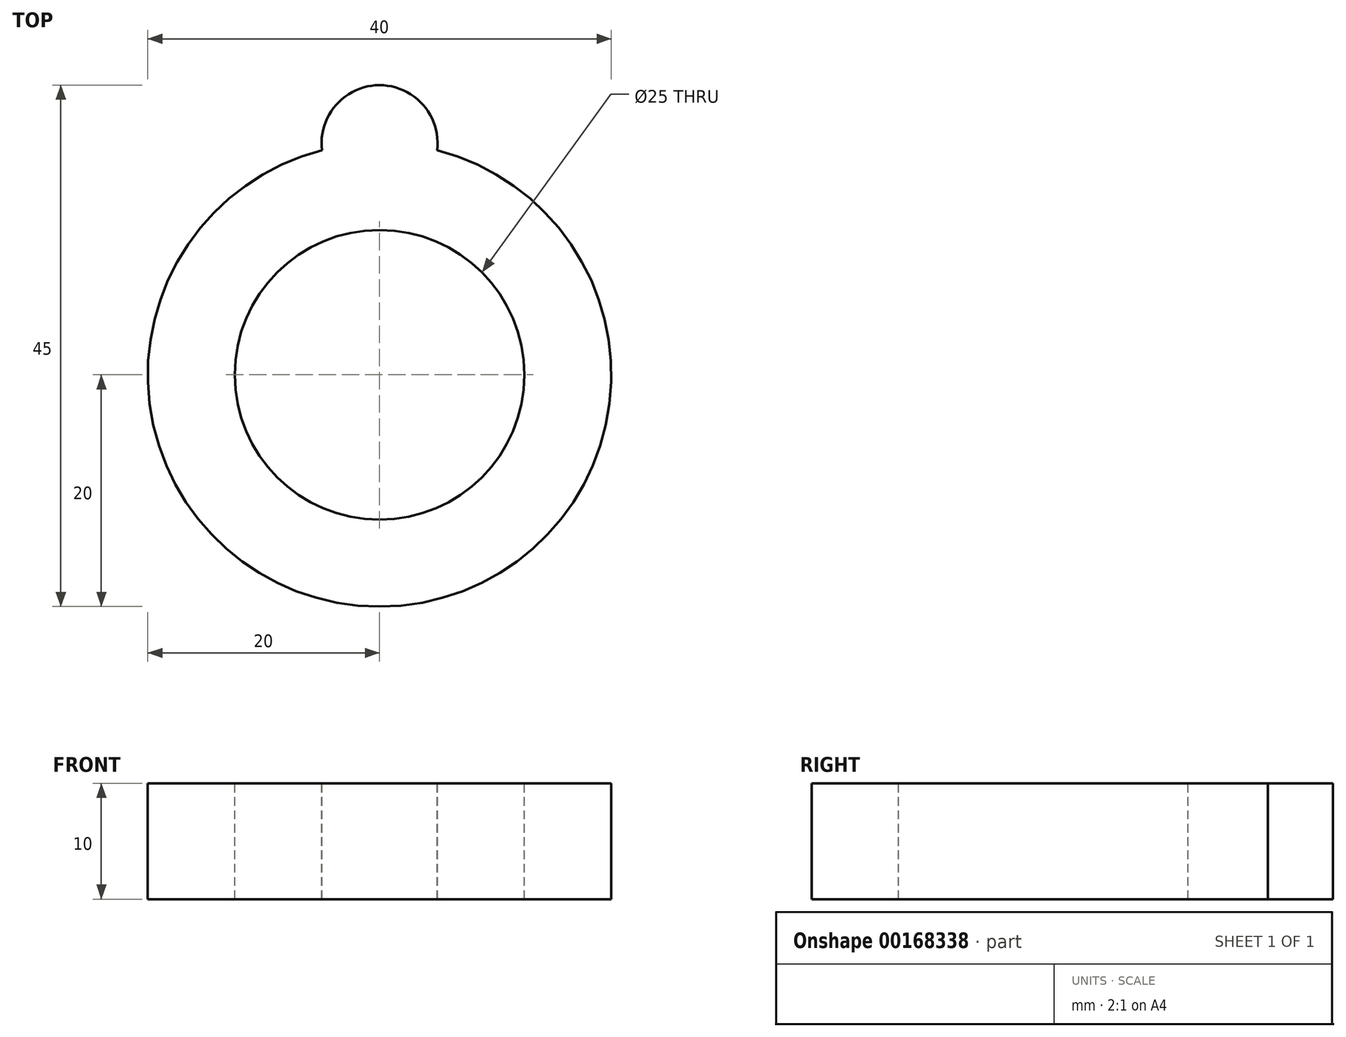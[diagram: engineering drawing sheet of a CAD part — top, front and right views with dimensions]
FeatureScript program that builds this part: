
annotation { "Feature Type Name" : "Feature", "Feature Type Description" : "" }
export const myFeature = defineFeature(function(context is Context, id is Id, definition is map)
    precondition{}
    {
        {
            var Q0;
            Q0=qCreatedBy(makeId("Top.planeOp"),FACE);
            var sketch = newSketch(context, id + "F0", { "sketchPlane" : qUnion([Q0])});
            skCircle(sketch, "E0", {"center": v(0, 0) * mm, "radius": 20 * mm});
            skSolve(sketch);
        }
        {
            var Q0;
            Q0=qSketchRegion(id+"F0",true);
            extrude(context, id + "F1", {"entities" : qUnion([Q0]), "depth" : 10 * mm});
        }
        {
            var Q0;
            Q0=makeQuery(id+"F1.opExtrude","CAP_FACE",FACE,{"disambiguationData":[OSD([sQuery(id+"F0.wireOp",EDGE,"E0")])],"isStart":false});
            var sketch = newSketch(context, id + "F2", { "sketchPlane" : qUnion([Q0])});
            skCircle(sketch, "E1", {"center": v(0, 0) * mm, "radius": 12.5 * mm});
            skSolve(sketch);
        }
        {
            var Q0;
            Q0=qSketchRegion(id+"F2",true);
            extrude(context, id + "F3", {"entities" : qUnion([Q0]), "operationType" : NewBodyOperationType.REMOVE, "oppositeDirection" : true, "depth" : 10 * mm});
        }
        {
            var Q0;
            Q0=makeQuery(id+"F1.opExtrude","CAP_FACE",FACE,{"disambiguationData":[OSD([sQuery(id+"F0.wireOp",EDGE,"E0")])],"isStart":false});
            var sketch = newSketch(context, id + "F4", { "sketchPlane" : qUnion([Q0])});
            skCircle(sketch, "E2", {"center": v(0, 20) * mm, "radius": 5 * mm});
            skSolve(sketch);
        }
        {
            var Q0;
            Q0 = qSketchRegion(id + "F4", true);
            var Q1;
            Q1=makeQuery(id+"F1.opExtrude","CAP_FACE",FACE,{"disambiguationData":[OSD([sQuery(id+"F0.wireOp",EDGE,"E0")])],"isStart":true});
            extrude(context, id + "F5", {"entities" : qUnion([Q0]), "operationType" : NewBodyOperationType.ADD, "endBound" : BoundingType.UP_TO_SURFACE, "oppositeDirection" : true, "endBoundEntityFace" : qUnion([Q1]), "depth" : 25 * mm});
        }
    });
